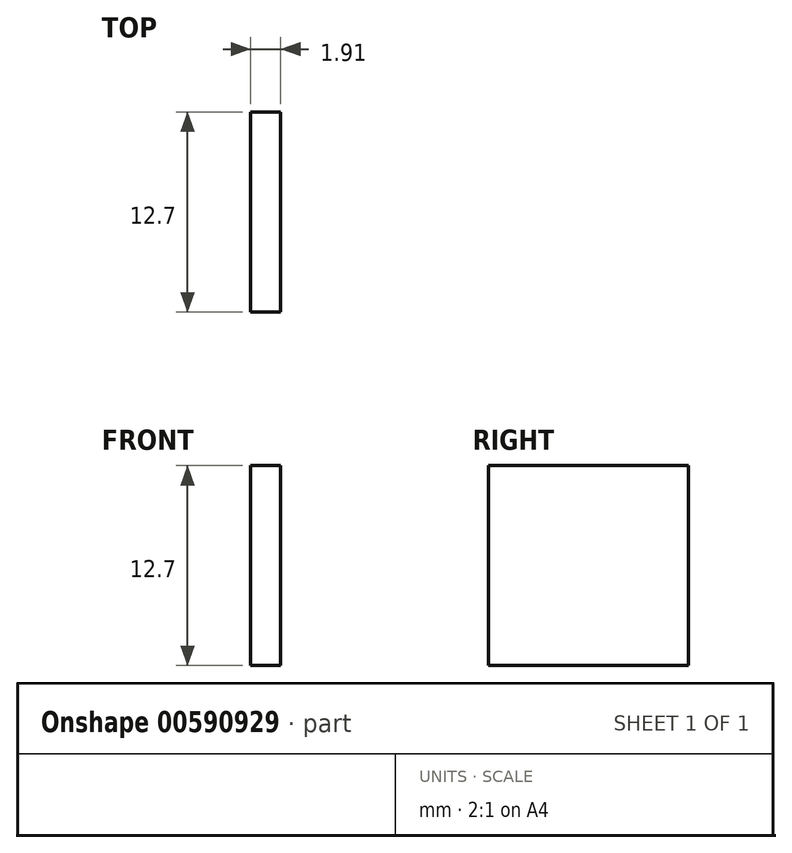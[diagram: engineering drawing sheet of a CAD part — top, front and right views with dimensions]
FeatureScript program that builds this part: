
annotation { "Feature Type Name" : "Feature", "Feature Type Description" : "" }
export const myFeature = defineFeature(function(context is Context, id is Id, definition is map)
    precondition{}
    {
        {
            var Q0;
            Q0=qCreatedBy(makeId("Right.planeOp"),FACE);
            var sketch = newSketch(context, id + "F0", { "sketchPlane" : qUnion([Q0])});
            skLineSegment(sketch, "E0.bottom", {"start": v(-40.9, 48.06) * mm, "end": v(-28.2, 48.06) * mm});
            skLineSegment(sketch, "E0.top", {"start": v(-40.9, 35.36) * mm, "end": v(-28.2, 35.36) * mm});
            skLineSegment(sketch, "E0.left", {"start": v(-40.9, 48.06) * mm, "end": v(-40.9, 35.36) * mm});
            skLineSegment(sketch, "E0.right", {"start": v(-28.2, 48.06) * mm, "end": v(-28.2, 35.36) * mm});
            skSolve(sketch);
        }
        {
            var Q0;
            Q0=makeQuery(id+"F0.imprint","IMPRINT",FACE,{"disambiguationData":[TD([[makeQuery(id+"F0.imprint","IMPRINT",EDGE,{"derivedFrom":sQuery(id+"F0.wireOp",EDGE,"E0.bottom")}),-1.0]])]});
            extrude(context, id + "F1", {"entities" : qUnion([Q0]), "depth" : 1.9 * mm, "offsetDistance" : 25.4 * mm});
        }
    });
